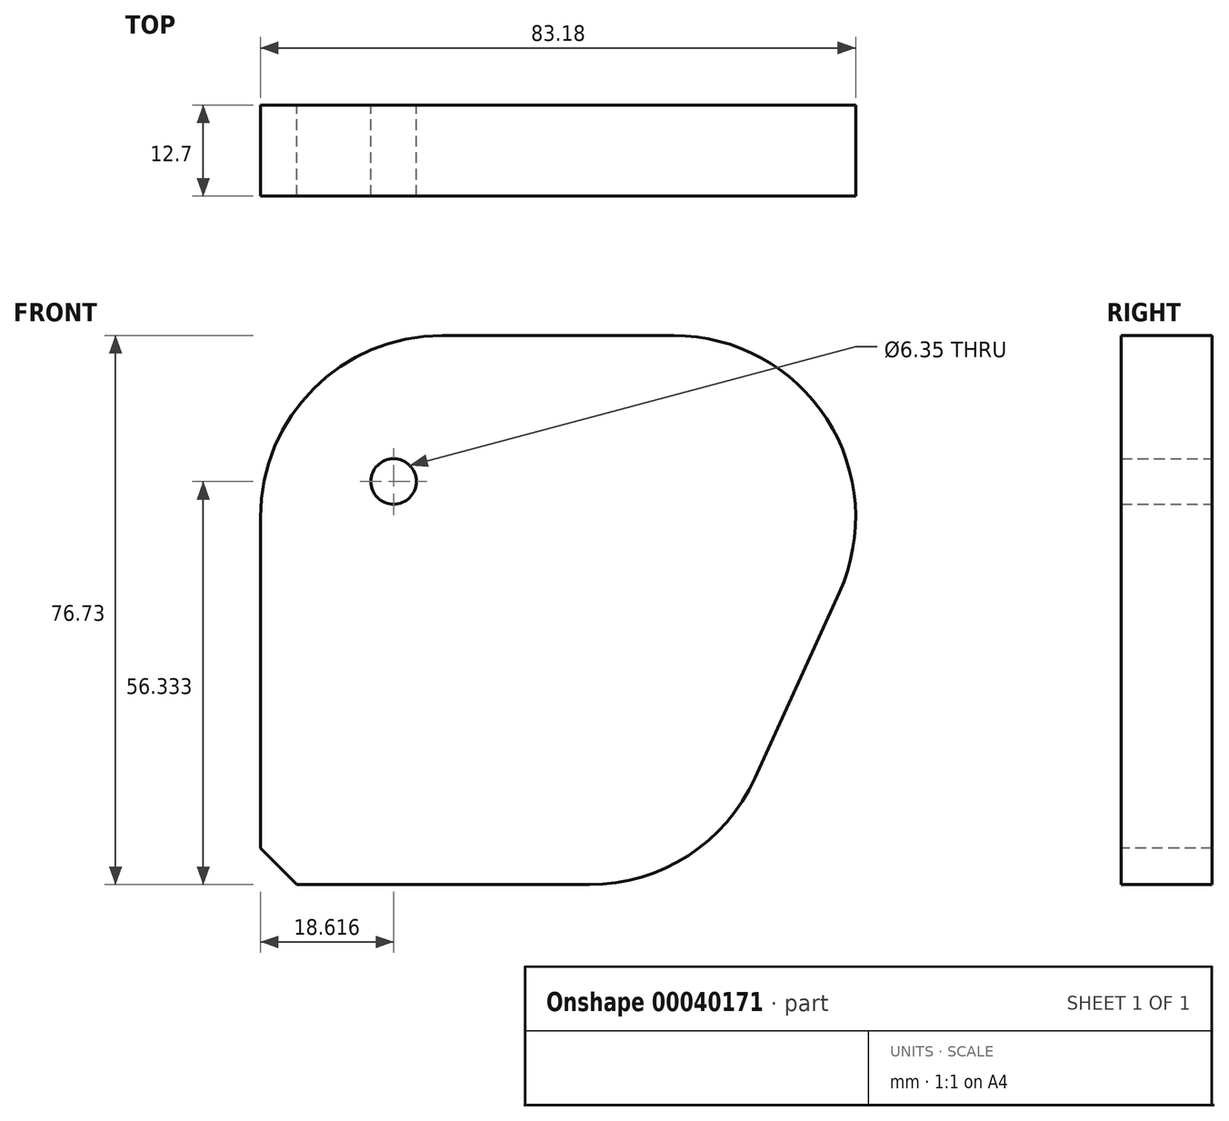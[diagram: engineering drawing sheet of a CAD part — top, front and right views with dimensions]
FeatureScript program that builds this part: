
annotation { "Feature Type Name" : "Feature", "Feature Type Description" : "" }
export const myFeature = defineFeature(function(context is Context, id is Id, definition is map)
    precondition{}
    {
        {
            var Q0;
            Q0=qCreatedBy(makeId("Front.planeOp"),FACE);
            var sketch = newSketch(context, id + "F0", { "sketchPlane" : qUnion([Q0])});
            skLineSegment(sketch, "E0", {"start": v(-69.33, 3.91) * mm, "end": v(-69.33, -47.42) * mm});
            skLineSegment(sketch, "E1", {"start": v(-43.93, 29.31) * mm, "end": v(-11.55, 29.31) * mm});
            skLineSegment(sketch, "E2", {"start": v(11.57, -6.59) * mm, "end": v(-0.2, -32.52) * mm});
            skLineSegment(sketch, "E3", {"start": v(-23.33, -47.42) * mm, "end": v(-69.33, -47.42) * mm});
            skPoint(sketch, "E4.visualSharp", {"position": v(-69.33, 29.31) * mm});
            skArc(sketch, "E4.filletArc", {"start": v(-43.93, 29.31) * mm, "mid": v(-61.89, 21.87) * mm, "end": v(-69.33, 3.91) * mm});
            skPoint(sketch, "E5.visualSharp", {"position": v(-6.97, -47.42) * mm});
            skArc(sketch, "E5.filletArc", {"start": v(-23.33, -47.42) * mm, "mid": v(-9.58, -43.37) * mm, "end": v(-0.2, -32.52) * mm});
            skPoint(sketch, "E6.visualSharp", {"position": v(27.88, 29.31) * mm});
            skArc(sketch, "E6.filletArc", {"start": v(11.57, -6.59) * mm, "mid": v(9.8, 17.67) * mm, "end": v(-11.55, 29.31) * mm});
            skSolve(sketch);
        }
        {
            var Q0;
            Q0=makeQuery(id+"F0.imprint","IMPRINT",FACE,{"disambiguationData":[TD([[makeQuery(id+"F0.imprint","IMPRINT",EDGE,{"derivedFrom":sQuery(id+"F0.wireOp",EDGE,"E0")}),1.0]])]});
            extrude(context, id + "F1", {"entities" : qUnion([Q0]), "depth" : 12.7 * mm});
        }
        {
            var Q0;
            Q0=makeQuery(id+"F1.opExtrude","CAP_FACE",FACE,{"disambiguationData":[OSD([sQuery(id+"F0.wireOp",EDGE,"E0"),sQuery(id+"F0.wireOp",EDGE,"E1"),sQuery(id+"F0.wireOp",EDGE,"E2"),sQuery(id+"F0.wireOp",EDGE,"E3"),sQuery(id+"F0.wireOp",EDGE,"E4.filletArc"),sQuery(id+"F0.wireOp",EDGE,"E5.filletArc"),sQuery(id+"F0.wireOp",EDGE,"E6.filletArc")])],"isStart":true});
            var sketch = newSketch(context, id + "F2", { "sketchPlane" : qUnion([Q0])});
            skPoint(sketch, "E7", {"position": v(58.21, -32.52) * mm});
            skPoint(sketch, "E8", {"position": v(19.99, -24.08) * mm});
            skPoint(sketch, "E9", {"position": v(50.71, 8.91) * mm});
            skPoint(sketch, "E10", {"position": v(22.77, 10.85) * mm});
            skSolve(sketch);
        }
        {
            var Q0;
            Q0=sQuery(id+"F2.wireOp",VERTEX,"E9");
            var Q1;
            Q1=makeQuery(id+"F1.opExtrude","SWEPT_BODY",BODY,{"disambiguationData":[OSD([sQuery(id+"F0.wireOp",EDGE,"E0"),sQuery(id+"F0.wireOp",EDGE,"E1"),sQuery(id+"F0.wireOp",EDGE,"E2"),sQuery(id+"F0.wireOp",EDGE,"E3"),sQuery(id+"F0.wireOp",EDGE,"E4.filletArc"),sQuery(id+"F0.wireOp",EDGE,"E5.filletArc"),sQuery(id+"F0.wireOp",EDGE,"E6.filletArc")])]});
            hole(context, id + "F3", {"style" : HoleStyle.SIMPLE, "holeDiameter" : 6.35 * mm, "endStyle" : HoleEndStyle.THROUGH, "locations" : qUnion([Q0]), "scope" : qUnion([Q1])});
        }
        {
            var Q0;
            Q0=makeQuery(id+"F1.opExtrude","SWEPT_EDGE",EDGE,{"disambiguationData":[OSD([sQuery(id+"F0.wireOp",EDGE,"E0"),sQuery(id+"F0.wireOp",EDGE,"E3")])]});
            chamfer(context, id + "F4", {"entities" : qUnion([Q0]), "width" : 5.08 * mm, "tangentPropagation" : true});
        }
    });
